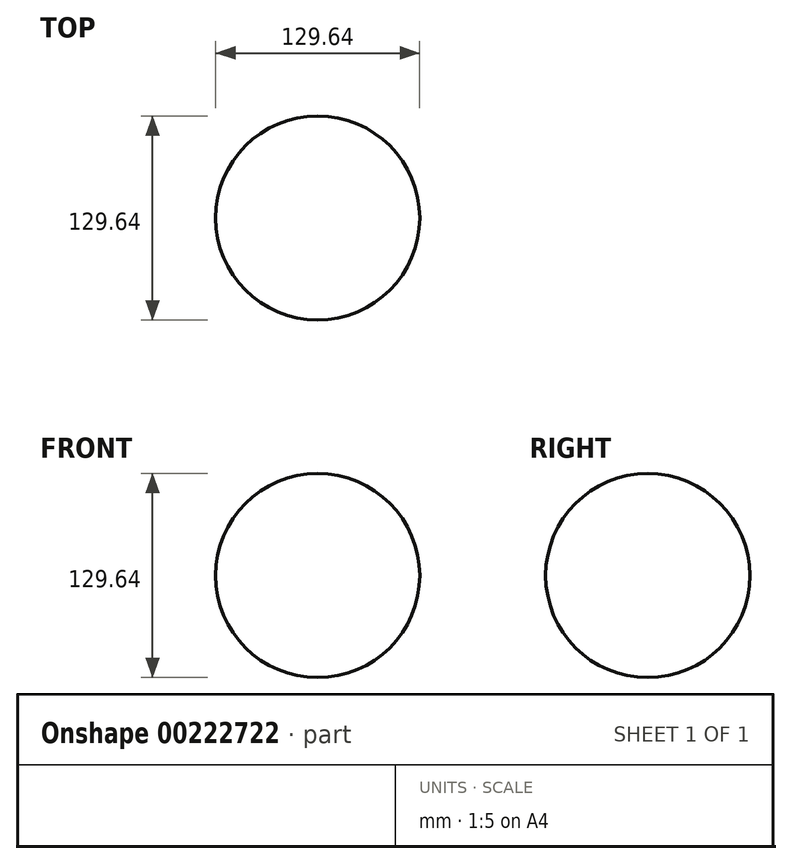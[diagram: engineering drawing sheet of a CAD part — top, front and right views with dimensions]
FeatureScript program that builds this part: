
annotation { "Feature Type Name" : "Feature", "Feature Type Description" : "" }
export const myFeature = defineFeature(function(context is Context, id is Id, definition is map)
    precondition{}
    {
        {
            var Q0;
            Q0=qCreatedBy(makeId("Top.planeOp"),FACE);
            var sketch = newSketch(context, id + "F0", { "sketchPlane" : qUnion([Q0])});
            skArc(sketch, "E0", {"start": v(0, 64.82) * mm, "mid": v(-64.82, 0) * mm, "end": v(0, -64.82) * mm});
            skLineSegment(sketch, "E1", {"start": v(0, -75.86) * mm, "end": v(0, 74.5) * mm});
            skSolve(sketch);
        }
        {
            var Q0;
            Q0=makeQuery(id+"F0.imprint","IMPRINT",FACE,{"disambiguationData":[TD([[makeQuery(id+"F0.imprint","IMPRINT",EDGE,{"derivedFrom":sQuery(id+"F0.wireOp",EDGE,"E0")}),1.0]])]});
            var Q1;
            Q1=sQuery(id+"F0.wireOp",EDGE,"E1");
            revolve(context, id + "F1", {"entities" : qUnion([Q0]), "axis" : qUnion([Q1]), "revolveType" : RevolveType.FULL});
        }
    });
